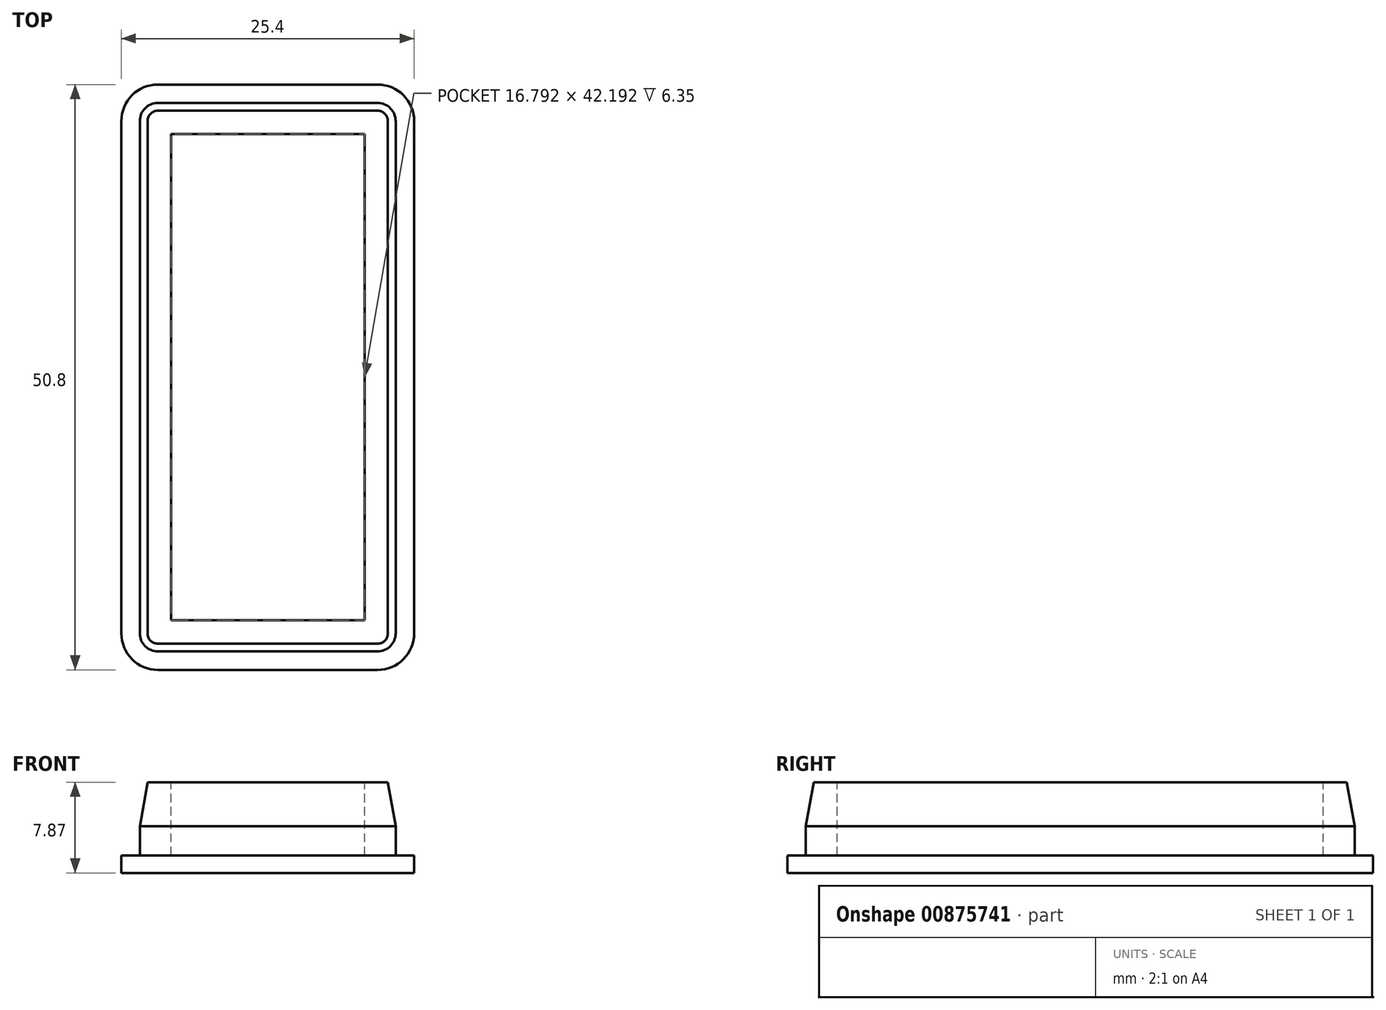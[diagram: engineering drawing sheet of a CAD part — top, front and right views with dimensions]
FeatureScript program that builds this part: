
annotation { "Feature Type Name" : "Feature", "Feature Type Description" : "" }
export const myFeature = defineFeature(function(context is Context, id is Id, definition is map)
    precondition{}
    {
        {
            var Q0;
            Q0=qCreatedBy(makeId("Top.planeOp"),FACE);
            var sketch = newSketch(context, id + "F0", { "sketchPlane" : qUnion([Q0])});
            skLineSegment(sketch, "E0.bottom", {"start": v(3.17, 0) * mm, "end": v(22.23, 0) * mm});
            skLineSegment(sketch, "E0.top", {"start": v(3.17, 50.8) * mm, "end": v(22.22, 50.8) * mm});
            skLineSegment(sketch, "E0.left", {"start": v(0, 3.18) * mm, "end": v(0, 47.62) * mm});
            skLineSegment(sketch, "E0.right", {"start": v(25.4, 3.18) * mm, "end": v(25.4, 47.62) * mm});
            skPoint(sketch, "E1.visualSharp", {"position": v(0, 0) * mm});
            skArc(sketch, "E1.filletArc", {"start": v(0, 3.17) * mm, "mid": v(0.93, 0.93) * mm, "end": v(3.17, 0) * mm});
            skPoint(sketch, "E2.visualSharp", {"position": v(0, 50.8) * mm});
            skArc(sketch, "E2.filletArc", {"start": v(3.17, 50.8) * mm, "mid": v(0.93, 49.87) * mm, "end": v(0, 47.62) * mm});
            skPoint(sketch, "E3.visualSharp", {"position": v(25.4, 50.8) * mm});
            skArc(sketch, "E3.filletArc", {"start": v(25.4, 47.62) * mm, "mid": v(24.47, 49.87) * mm, "end": v(22.22, 50.8) * mm});
            skPoint(sketch, "E4.visualSharp", {"position": v(25.4, 0) * mm});
            skArc(sketch, "E4.filletArc", {"start": v(22.23, 0) * mm, "mid": v(24.47, 0.93) * mm, "end": v(25.4, 3.18) * mm});
            skSolve(sketch);
        }
        {
            var Q0;
            Q0=makeQuery(id+"F0.imprint","IMPRINT",FACE,{"disambiguationData":[TD([[makeQuery(id+"F0.imprint","IMPRINT",EDGE,{"derivedFrom":sQuery(id+"F0.wireOp",EDGE,"E0.bottom")}),1.0]])]});
            extrude(context, id + "F1", {"entities" : qUnion([Q0]), "depth" : 1.52 * mm, "offsetDistance" : 25.4 * mm});
        }
        {
            var Q0;
            Q0=makeQuery(id+"F1.opExtrude","CAP_FACE",FACE,{"disambiguationData":[OSD([sQuery(id+"F0.wireOp",EDGE,"E0.bottom"),sQuery(id+"F0.wireOp",EDGE,"E0.top"),sQuery(id+"F0.wireOp",EDGE,"E0.left"),sQuery(id+"F0.wireOp",EDGE,"E0.right"),sQuery(id+"F0.wireOp",EDGE,"E1.filletArc"),sQuery(id+"F0.wireOp",EDGE,"E2.filletArc"),sQuery(id+"F0.wireOp",EDGE,"E3.filletArc"),sQuery(id+"F0.wireOp",EDGE,"E4.filletArc")])],"isStart":false});
            var sketch = newSketch(context, id + "F2", { "sketchPlane" : qUnion([Q0])});
            skArc(sketch, "E5.0", {"start": v(23.8, 47.62) * mm, "mid": v(23.34, 48.74) * mm, "end": v(22.22, 49.2) * mm});
            skLineSegment(sketch, "E5.1", {"start": v(23.8, 3.18) * mm, "end": v(23.8, 47.62) * mm});
            skLineSegment(sketch, "E5.2", {"start": v(22.22, 49.2) * mm, "end": v(3.17, 49.2) * mm});
            skArc(sketch, "E5.3", {"start": v(22.23, 1.6) * mm, "mid": v(23.34, 2.06) * mm, "end": v(23.8, 3.18) * mm});
            skArc(sketch, "E5.4", {"start": v(3.17, 49.2) * mm, "mid": v(2.06, 48.74) * mm, "end": v(1.6, 47.62) * mm});
            skLineSegment(sketch, "E5.5", {"start": v(1.6, 47.62) * mm, "end": v(1.6, 3.18) * mm});
            skArc(sketch, "E5.6", {"start": v(1.6, 3.18) * mm, "mid": v(2.06, 2.06) * mm, "end": v(3.17, 1.6) * mm});
            skLineSegment(sketch, "E5.7", {"start": v(3.17, 1.6) * mm, "end": v(22.23, 1.6) * mm});
            skSolve(sketch);
        }
        {
            var Q0;
            Q0=makeQuery(id+"F2.imprint","IMPRINT",FACE,{"disambiguationData":[TD([[makeQuery(id+"F2.imprint","IMPRINT",EDGE,{"derivedFrom":sQuery(id+"F2.wireOp",EDGE,"E5.0")}),1.0]])]});
            extrude(context, id + "F3", {"entities" : qUnion([Q0]), "operationType" : NewBodyOperationType.ADD, "depth" : 2.54 * mm, "offsetDistance" : 25.4 * mm});
        }
        {
            var Q0;
            Q0=makeQuery(id+"F3.opExtrude","CAP_FACE",FACE,{"disambiguationData":[OSD([sQuery(id+"F2.wireOp",EDGE,"E5.0"),sQuery(id+"F2.wireOp",EDGE,"E5.1"),sQuery(id+"F2.wireOp",EDGE,"E5.2"),sQuery(id+"F2.wireOp",EDGE,"E5.3"),sQuery(id+"F2.wireOp",EDGE,"E5.4"),sQuery(id+"F2.wireOp",EDGE,"E5.5"),sQuery(id+"F2.wireOp",EDGE,"E5.6"),sQuery(id+"F2.wireOp",EDGE,"E5.7")])],"isStart":false});
            extrude(context, id + "F4", {"entities" : qUnion([Q0]), "operationType" : NewBodyOperationType.ADD, "depth" : 3.8 * mm, "offsetDistance" : 25.4 * mm, "hasDraft" : true, "draftAngle" : 10 * degree, "draftPullDirection" : true});
        }
        {
            var Q0;
            Q0=makeQuery(id+"F4.opExtrude","CAP_FACE",FACE,{"disambiguationData":[OSD([sQuery(id+"F2.wireOp",EDGE,"E5.0"),sQuery(id+"F2.wireOp",EDGE,"E5.1"),sQuery(id+"F2.wireOp",EDGE,"E5.2"),sQuery(id+"F2.wireOp",EDGE,"E5.3"),sQuery(id+"F2.wireOp",EDGE,"E5.4"),sQuery(id+"F2.wireOp",EDGE,"E5.5"),sQuery(id+"F2.wireOp",EDGE,"E5.6"),sQuery(id+"F2.wireOp",EDGE,"E5.7")])],"isStart":false});
            var sketch = newSketch(context, id + "F5", { "sketchPlane" : qUnion([Q0])});
            skLineSegment(sketch, "E6.0", {"start": v(4.3, 47.62) * mm, "end": v(4.3, 3.18) * mm});
            skArc(sketch, "E6.1", {"start": v(3.17, 46.5) * mm, "mid": v(3.97, 46.83) * mm, "end": v(4.3, 47.62) * mm});
            skArc(sketch, "E6.2", {"start": v(4.3, 3.18) * mm, "mid": v(3.97, 3.97) * mm, "end": v(3.17, 4.3) * mm});
            skLineSegment(sketch, "E6.3", {"start": v(22.22, 46.5) * mm, "end": v(3.17, 46.5) * mm});
            skLineSegment(sketch, "E6.4", {"start": v(3.17, 4.3) * mm, "end": v(22.23, 4.3) * mm});
            skArc(sketch, "E6.5", {"start": v(22.23, 4.3) * mm, "mid": v(21.43, 3.97) * mm, "end": v(21.1, 3.18) * mm});
            skLineSegment(sketch, "E6.6", {"start": v(21.1, 3.18) * mm, "end": v(21.1, 47.62) * mm});
            skArc(sketch, "E6.7", {"start": v(21.1, 47.62) * mm, "mid": v(21.43, 46.83) * mm, "end": v(22.22, 46.5) * mm});
            skSolve(sketch);
        }
        {
            var Q0;
            {var subQ0=sQuery(id+"F5.wireOp",EDGE,"E6.3");var subQ1=sQuery(id+"F5.wireOp",EDGE,"E6.0");var subQ2=makeQuery(id+"F5.imprint","INTERSECT",VERTEX,{"derivedFrom":[subQ1,subQ0]});Q0=makeQuery(id+"F5.imprint","IMPRINT",FACE,{"disambiguationData":[TD([[makeQuery(id+"F5.imprint","IMPRINT",EDGE,{"disambiguationData":[TD([[subQ2,-1.0]])],"derivedFrom":subQ1}),1.0]])]});}
            extrude(context, id + "F6", {"entities" : qUnion([Q0]), "operationType" : NewBodyOperationType.REMOVE, "oppositeDirection" : true, "depth" : 6.35 * mm, "offsetDistance" : 25.4 * mm});
        }
    });
